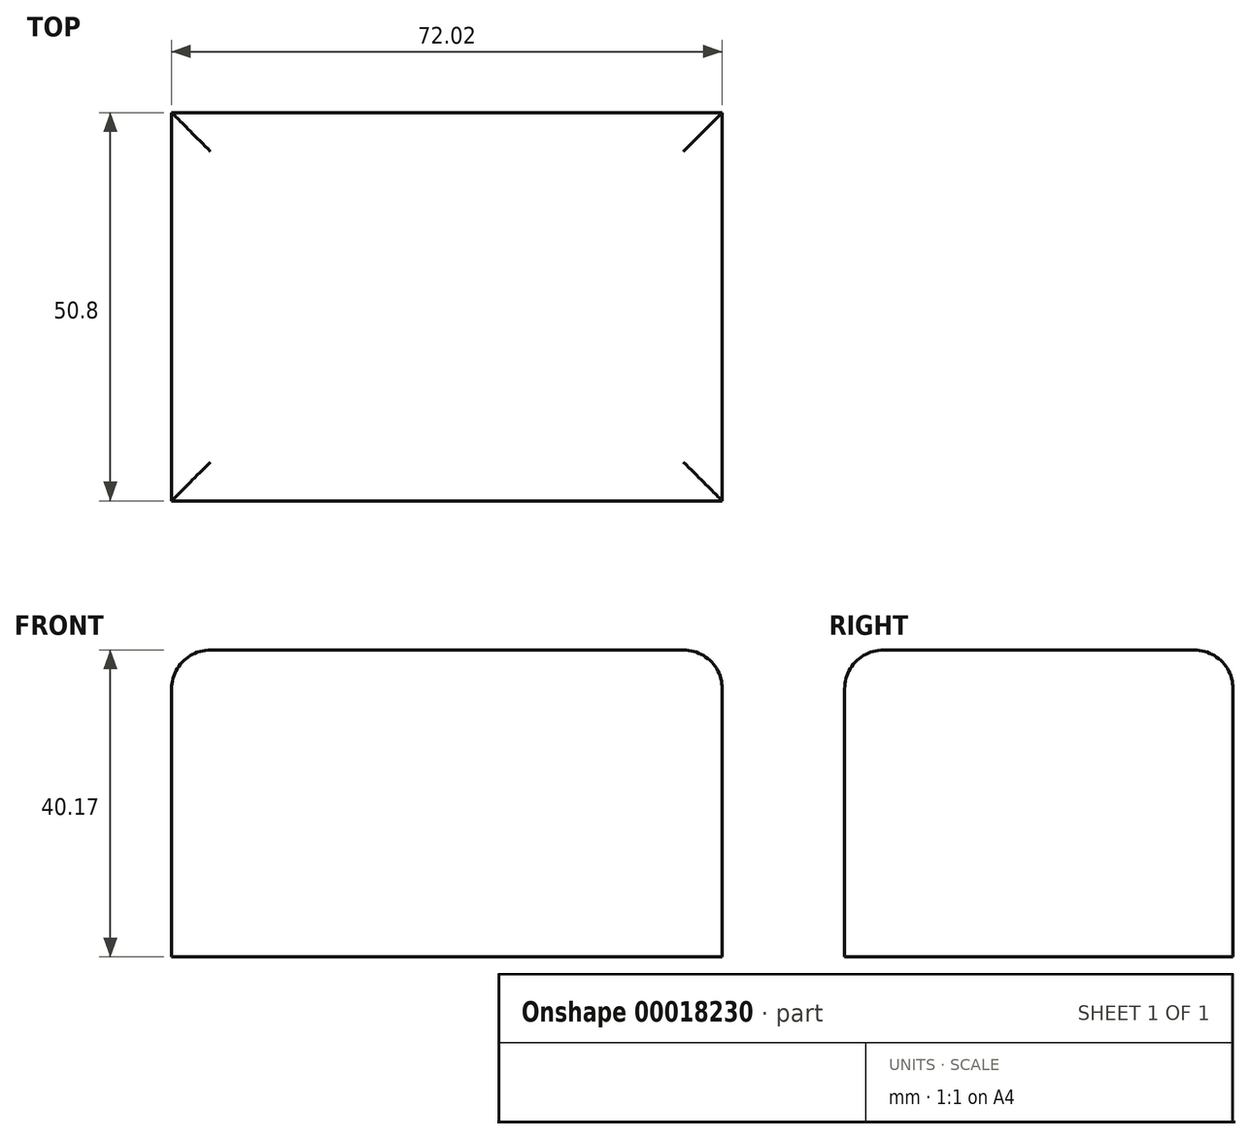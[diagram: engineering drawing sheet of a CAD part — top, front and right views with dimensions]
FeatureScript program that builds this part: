
annotation { "Feature Type Name" : "Feature", "Feature Type Description" : "" }
export const myFeature = defineFeature(function(context is Context, id is Id, definition is map)
    precondition{}
    {
        {
            var Q0;
            Q0=qCreatedBy(makeId("Front.planeOp"),FACE);
            var sketch = newSketch(context, id + "F0", { "sketchPlane" : qUnion([Q0])});
            skLineSegment(sketch, "E0.bottom", {"start": v(-33.16, 0) * mm, "end": v(38.86, 0) * mm});
            skLineSegment(sketch, "E0.top", {"start": v(-33.16, 40.17) * mm, "end": v(38.86, 40.17) * mm});
            skLineSegment(sketch, "E0.left", {"start": v(-33.16, 0) * mm, "end": v(-33.16, 40.17) * mm});
            skLineSegment(sketch, "E0.right", {"start": v(38.86, 0) * mm, "end": v(38.86, 40.17) * mm});
            skSolve(sketch);
        }
        {
            var Q0;
            Q0=makeQuery(id+"F0.imprint","IMPRINT",FACE,{"disambiguationData":[TD([[makeQuery(id+"F0.imprint","IMPRINT",EDGE,{"derivedFrom":sQuery(id+"F0.wireOp",EDGE,"E0.bottom")}),1.0]])]});
            extrude(context, id + "F1", {"entities" : qUnion([Q0]), "depth" : 50.8 * mm});
        }
        {
            var Q0;
            Q0=makeQuery(id+"F1.opExtrude","SWEPT_EDGE",EDGE,{"disambiguationData":[OSD([sQuery(id+"F0.wireOp",EDGE,"E0.top"),sQuery(id+"F0.wireOp",EDGE,"E0.right")])]});
            var Q1;
            Q1=makeQuery(id+"F1.opExtrude","CAP_EDGE",EDGE,{"disambiguationData":[OSD([sQuery(id+"F0.wireOp",EDGE,"E0.top")])],"isStart":false});
            var Q2;
            Q2=makeQuery(id+"F1.opExtrude","SWEPT_EDGE",EDGE,{"disambiguationData":[OSD([sQuery(id+"F0.wireOp",EDGE,"E0.top"),sQuery(id+"F0.wireOp",EDGE,"E0.left")])]});
            var Q3;
            Q3=makeQuery(id+"F1.opExtrude","CAP_EDGE",EDGE,{"disambiguationData":[OSD([sQuery(id+"F0.wireOp",EDGE,"E0.top")])],"isStart":true});
            fillet(context, id + "F2", {"entities" : qUnion([Q0, Q1, Q2, Q3]), "radius" : 5.08 * mm, "tangentPropagation" : true, "allowEdgeOverflow" : false});
        }
    });
